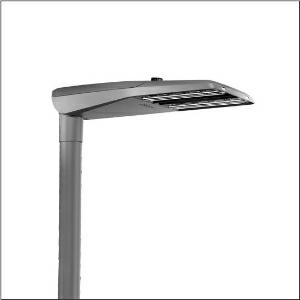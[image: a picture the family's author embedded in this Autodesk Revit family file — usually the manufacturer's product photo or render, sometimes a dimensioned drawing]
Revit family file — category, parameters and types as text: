
# Revit family: streetlight_sl_11_iq_midi___st1_2a_5xc3a41u08me_4bff
name_source: partatom
category: Lighting Fixtures
units: mm (PartAtom-declared; Revit-internal decimal feet)

## family parameters
Cut with Voids When Loaded = No
Host = Face
Light Source = No
Part Type = Normal
Room Calculation Point = No
Round Connector Dimension = Use Diameter
Shared = No

## types (1)
- --- (1 x LED, 18900 lm, 122.6 W, 4000K)
    Apparent Load = 123 VA
    CIE Flux Codes = 32 70 96 100 100
    Color Rendering = 70
    Color Temperature = 4000K
    Default Elevation = 1800 mm
    Description = Streetlight SL 11 iQ midi, mast luminaire, primary light control with 3 zone facetted reflector, of plastic, silver coated, highly specular, primary optical cover: cover, of PMMA, transparent, light distribution: ST1.2a, light emission: direct distribution, primary light characteristic: asymmetric, installation type: post-top, side-entry, lamps: LED, High Power LED, rated values: 18.900lm | 122,6W | 154,2lm/W (begin service life); end service life: 18.900lm | 130,2W; at 50% lumin. flux: 9.450lm | 56,3W | 167,9lm/W, colour temperature: 4000K, colour rendering: CRI > 70, light colour: 740, light setting 1 begin service life: 100% | 18.900lm | 122,6W | 154,2lm/W | 4.000K, light setting 1 end service life: 130,2W, further light settings possible, control: pre-setting: logarithmic dimming characteristic, Street-Remote, Auto-Match, Temp-Guard, Lumen-Switch, Night-Set, Smart-Wire, Light-Fading, Desk-Remote (wireless, voltage-free reading and setting of iQ features in the workshop via application-optimized NFC function/RFID function), optimised constant luminous flux control (CLO 2.0), with cable H07RN-F 3x 1.5mm², mains connection: 230..240V, AC, 50/60Hz, connection cable pre-assembled, cable length: 12,5m, luminaire housing, of diecast aluminium, powder-coated, SITECO metallic grey (DB 702S), please order mast flange separately, inclination adjustable without tools: 0°, 5°, 10°, 15° (post-top) | 0°, -5°, -10°, -15° (side-entry), sealing non-destructively replaceable, multi-level sealing system, length: 780mm, width: 376mm, height: 118mm, mast flange for spigot size: 42mm (side-entry): 5XC10008XM4, 60/48mm (side-entry/post-top): 5XC10108XM2, 76/60mm (side-entry/post-top): 5XC10108XM1, equipment: Power, Smart Interface below, protection rating (complete): IP66, insulation class (complete): insulation class II (safety insulation), certification: CE, ENEC, ENEC+, VDE, UKCA, impact resistance: IK10, permissible operating ambient temperature for outdoor applications: -25..+50°C, standard-compliant lighting for roads and squares, Environmental Product Declaration (EPD) tested and certified by an independent institute, packaging unit: 1 piece

Light Distribution: ST1.2a
    Height = 118 mm
    Lamp = 1 x LED
    Lamp Light Flux = 18900 lm
    Lamp Power = 122.6 W
    Lamp count = 1
    Length = 780 mm
    Luminous efficacy = 154 lm/W
    Manufacturer = Siteco
    ModVariant = No
    Model = 5XC3A41U08ME
    Number of Poles = 1
    OnlyDefault = Yes
    Power Factor = 1
    Product Name = Streetlight SL 11 iQ midi | ST1.2a
    Product group = mast luminaire | pylon top
    ProductGroupID = 6100
    Protection Class = Protection class II
    Protection Degree = IP 66
    RLX_Detail_Level = 1
    RLX_Emergency_Light_Flux = 0 lm
    RLX_Emergency_Type = 0
    RLX_Emergency_Type_DB = No
    RlxData = <blob elided: 70013 chars, md5=faf43b0b>
    Socket = socket
    Standby Power = 0 W
    System Light Flux = 18900 lm
    System Power = 123 W
    Type Comments = factory setting: luminous flux: 100 % | dim-lin: 254 | 552 mA
    Type Image = l_1005968.jpg
    URL = http://relux.com
    VarID = @adj_132613
    Voltage = 0 V
    Weight = 0.00 kg
    Width = 376 mm

## geometry (parser evidence)
native form markers: Blend x4, Sweep x8
no freeform markers — native parametric forms only
